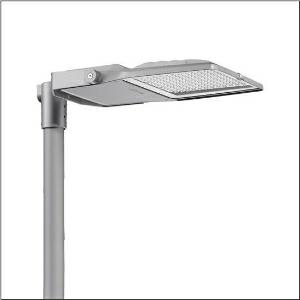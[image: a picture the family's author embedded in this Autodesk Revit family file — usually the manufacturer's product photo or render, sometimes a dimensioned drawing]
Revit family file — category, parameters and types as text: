
# Revit family: floodlight_fl_21_midi___pl33t_5xa7786f2f3a_5712
name_source: partatom
category: Lighting Fixtures
units: mm (PartAtom-declared; Revit-internal decimal feet)

## family parameters
Cut with Voids When Loaded = No
Host = Face
Light Source = No
Part Type = Normal
Room Calculation Point = No
Round Connector Dimension = Use Diameter
Shared = No

## types (1)
- --- (1 x LED, 35340 lm, 271.6 W, 3000K)
    Apparent Load = 272 VA
    CIE Flux Codes = 26 75 99 100 100
    Color Rendering = 70
    Color Temperature = 3000K
    Default Elevation = 1800 mm
    Description = Floodlight FL 21 midi, floodlight, primary light control with lens, of PMMA, primary optical cover: protective disc, of toughened safety glass, transparent, light distribution: PL33T, light emission: direct distribution, installation type: surface-mounted, LED, High Power LED, rated luminous flux: 35.340lm, luminous efficacy: 130lm/W, light colour: 730, colour temperature: 3000K, control gear: Smart Interface (Zhaga), control: flexible luminous flux parameterisation, time-dependent luminous flux control, constant luminous flux control, overheat protection, pre-setting: logarithmic dimming characteristic, with terminal, 6-pole, mains connection: 220..240V, AC, 50/60Hz, start of lifetime: 272W, end of service life: 287W, reduction: 123W, luminaire housing, of diecast aluminium, powder-coated, SITECO metallic grey (DB 702S), corrosivity category C5 mid according to DIN EN ISO 12944, suitable for swimming pools, chlorine-resistant, sealing non-destructively replaceable, please order mast flange separately, mast bracket, of steel, galvanised, powder-coated, SITECO metallic grey (DB 702S), Smart Interface below and above, protection rating (complete): IP66, insulation class (complete): insulation class II (safety insulation), certification: CE, ENEC, VDE, protection symbol: D, impact resistance: IK08, permissible operating ambient temperature: -40..+40°C, permissible operating ambient temperature for outdoor applications: -40..+50°C, standard: DIN EN 12944, LABS conformity tested according to VDMA 24364:2018-05, packaging unit: 1 piece

Light Distribution: PL33T
    Height = 76 mm
    Lamp = 1 x LED
    Lamp Light Flux = 35340 lm
    Lamp Power = 271.6 W
    Lamp count = 1
    Length = 657 mm
    Luminous efficacy = 130 lm/W
    Manufacturer = Siteco
    ModVariant = No
    Model = 5XA7786F2F3A
    Number of Poles = 1
    OnlyDefault = Yes
    Power Factor = 1
    Product Name = Floodlight FL 21 midi | PL33T
    Product group = floodlight | pylon annexe
    ProductGroupID = 6201
    Protection Class = Protection class II
    Protection Degree = IP 66
    RLX_Detail_Level = 1
    RLX_Emergency_Light_Flux = 0 lm
    RLX_Emergency_Type = 0
    RLX_Emergency_Type_DB = No
    RlxData = <blob elided: 153661 chars, md5=dfa8d8ff>
    Socket = socket
    Standby Power = 0 W
    System Light Flux = 35340 lm
    System Power = 272 W
    Type Comments = factory setting: luminous flux: 100 % | dim-lin: 254 | 620 mA
    Type Image = l_1007123.jpg
    URL = http://relux.com
    VarID = @adj_149887
    Voltage = 0 V
    Weight = 0.00 kg
    Width = 442 mm

## geometry (parser evidence)
native form markers: Blend x4, Sweep x12
no freeform markers — native parametric forms only
